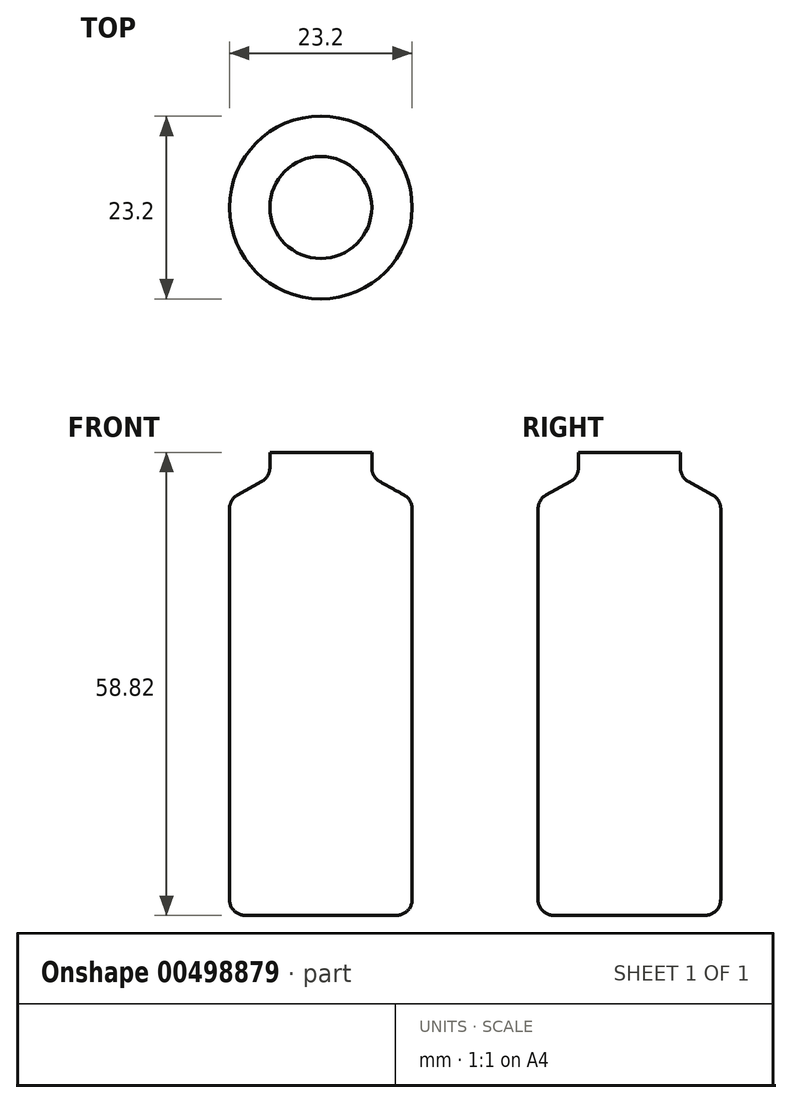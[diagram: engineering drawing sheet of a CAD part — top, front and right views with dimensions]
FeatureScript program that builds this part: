
annotation { "Feature Type Name" : "Feature", "Feature Type Description" : "" }
export const myFeature = defineFeature(function(context is Context, id is Id, definition is map)
    precondition{}
    {
        {
            var Q0;
            Q0=qCreatedBy(makeId("Front.planeOp"),FACE);
            var sketch = newSketch(context, id + "F0", { "sketchPlane" : qUnion([Q0])});
            skLineSegment(sketch, "E0", {"start": v(0, 38.3) * mm, "end": v(0, -20.52) * mm});
            skLineSegment(sketch, "E1", {"start": v(0, -20.52) * mm, "end": v(-9.6, -20.52) * mm});
            skLineSegment(sketch, "E2", {"start": v(-11.6, -18.52) * mm, "end": v(-11.6, 31.13) * mm});
            skLineSegment(sketch, "E3", {"start": v(0, 38.3) * mm, "end": v(-6.48, 38.3) * mm});
            skLineSegment(sketch, "E4", {"start": v(-6.48, 38.3) * mm, "end": v(-6.48, 36.33) * mm});
            skLineSegment(sketch, "E5", {"start": v(-7.5, 34.58) * mm, "end": v(-10.57, 32.87) * mm});
            skPoint(sketch, "E6.visualSharp", {"position": v(-6.48, 35.15) * mm});
            skArc(sketch, "E6.filletArc", {"start": v(-7.5, 34.58) * mm, "mid": v(-6.75, 35.31) * mm, "end": v(-6.48, 36.33) * mm});
            skPoint(sketch, "E7.visualSharp", {"position": v(-11.6, 32.3) * mm});
            skArc(sketch, "E7.filletArc", {"start": v(-10.57, 32.87) * mm, "mid": v(-11.33, 32.14) * mm, "end": v(-11.6, 31.13) * mm});
            skPoint(sketch, "E8.visualSharp", {"position": v(-11.6, -20.52) * mm});
            skArc(sketch, "E8.filletArc", {"start": v(-11.6, -18.52) * mm, "mid": v(-11.02, -19.94) * mm, "end": v(-9.6, -20.52) * mm});
            skSolve(sketch);
        }
        {
            var Q0;
            Q0=makeQuery(id+"F0.imprint","IMPRINT",FACE,{"disambiguationData":[TD([[makeQuery(id+"F0.imprint","IMPRINT",EDGE,{"derivedFrom":sQuery(id+"F0.wireOp",EDGE,"E0")}),-1.0]])]});
            var sketch = newSketch(context, id + "F1", { "sketchPlane" : qUnion([Q0])});
            skSolve(sketch);
        }
        {
            var Q0;
            Q0=makeQuery(id+"F1.imprint","IMPRINT",FACE,{"disambiguationData":[TD([[makeQuery(id+"F1.imprint","IMPRINT",EDGE,{"derivedFrom":makeQuery(id+"F0.imprint","IMPRINT",EDGE,{"derivedFrom":sQuery(id+"F0.wireOp",EDGE,"E0")})}),-1.0]])]});
            var Q1;
            Q1=sQuery(id+"F0.wireOp",EDGE,"E0");
            revolve(context, id + "F2", {"entities" : qUnion([Q0]), "axis" : qUnion([Q1]), "revolveType" : RevolveType.FULL});
        }
    });
